# Revit family: Screen_Window_SereneSeries_PhantomScreens
name_source: partatom
category: Windows
revit_build: Autodesk Revit 2017 (Build: 20160225_1515(x64)
units: mm (PartAtom-declared; Revit-internal decimal feet)

## family parameters
Always vertical = Yes
Cut with Voids When Loaded = No
Host = Wall
OmniClass Number = 23.30.60.21
OmniClass Title = Insect Screens
Room Calculation Point = No
Shared = No

## types (1)
- Type as Specified
    Aluminum Housing = Dark Acacia
    Aluminum Slide Bar = Dark Acacia
    Aluminum Track = Dark Acacia
    Assembly Code = B2020400
    Construction Details = http://www.arcat.com
    Default Sill Height = 3' - 0"
    Description = Phantom Screens Serene Series Screen
    Housing Depth = 0' - 2 5/16"
    Housing Height = 0' - 2 1/8"
    Installation-Fabrication = http://www.phantomscreens.com
    Keynote = 08 11 00
    Manufacturer = Phantom Screens
    Manufacturer Fax = 604-855-7834
    Manufacturer Website = http://www.phantomscreens.com
    Model = Serene Series
    Product Data = http://www.arcat.com
    Product Properties = http://www.phantomscreens.com
    Revision = R1_08-2016
    Sales Information = http://www.phantomscreens.com
    Screen = Suntex 80 - Charcoal
    Screen Thickness = 0' - 0 1/32"
    Slide Bar Depth = 0' - 0 23/32"
    Slide Bar Height = 0' - 1 13/32"
    Specification = http://www.phantomscreens.com
    Track Depth = 0' - 0 29/32"
    URL = http://www.phantomscreens.com
    Wall Closure = By host

## geometry (parser evidence)
native form markers: Sweep x1
no freeform markers — native parametric forms only
